# Revit family: 3461A_NX_Dry_Contact_Interface_Module
name_source: partatom
category: Communication Devices
revit_build: Autodesk Revit 2014 (Build: 20130308_1515(x64)
units: mm (PartAtom-declared; Revit-internal decimal feet)

## types (1)
- 3461A_NX_Dry_Contact_Interface_Module
    Apparent Load = 0 VA
    Assembly Code = D5090
    Black Material = Paint - Hubbell - Black Matte Textured
    Default Elevation = 48 "
    Description = It provides a simple way to incorporate standard dry contact inputs and outputs into the NX control
    Features = Programmable from the NX Area Controller
• Six dry contact inputs with pilots
• Accommodates 2 and 3 wire inputs (momentary or maintained)
• Six Form-C dry contact outputs
• Removable terminal blocks for easy connections
• DIN rail mounting in the NX Accessory Enclosure
• Requires the NX Device Network Interface Module for connection to
 the HubbNET network
    Green Element = Plastic - Hubbell - Green
    Manufacturer = Hubbell Control Solutions
    Model = NX Dry Contact Module
    Product Documentation Link = https://hubbellcdn.com
    Product Page URL = https://www.hubbell.com
    Steel = Metal-Hubbell-Galvanized_Steel
    Type Comments = NX Dry Contact Module
    URL = https://www.hubbell.com
    Voltage = 24 V
    Warranty = 5-Years Warranty
    White Element = Glass, White, High Luminance

## geometry (parser evidence)
native form markers: Sweep x1
no freeform markers — native parametric forms only
